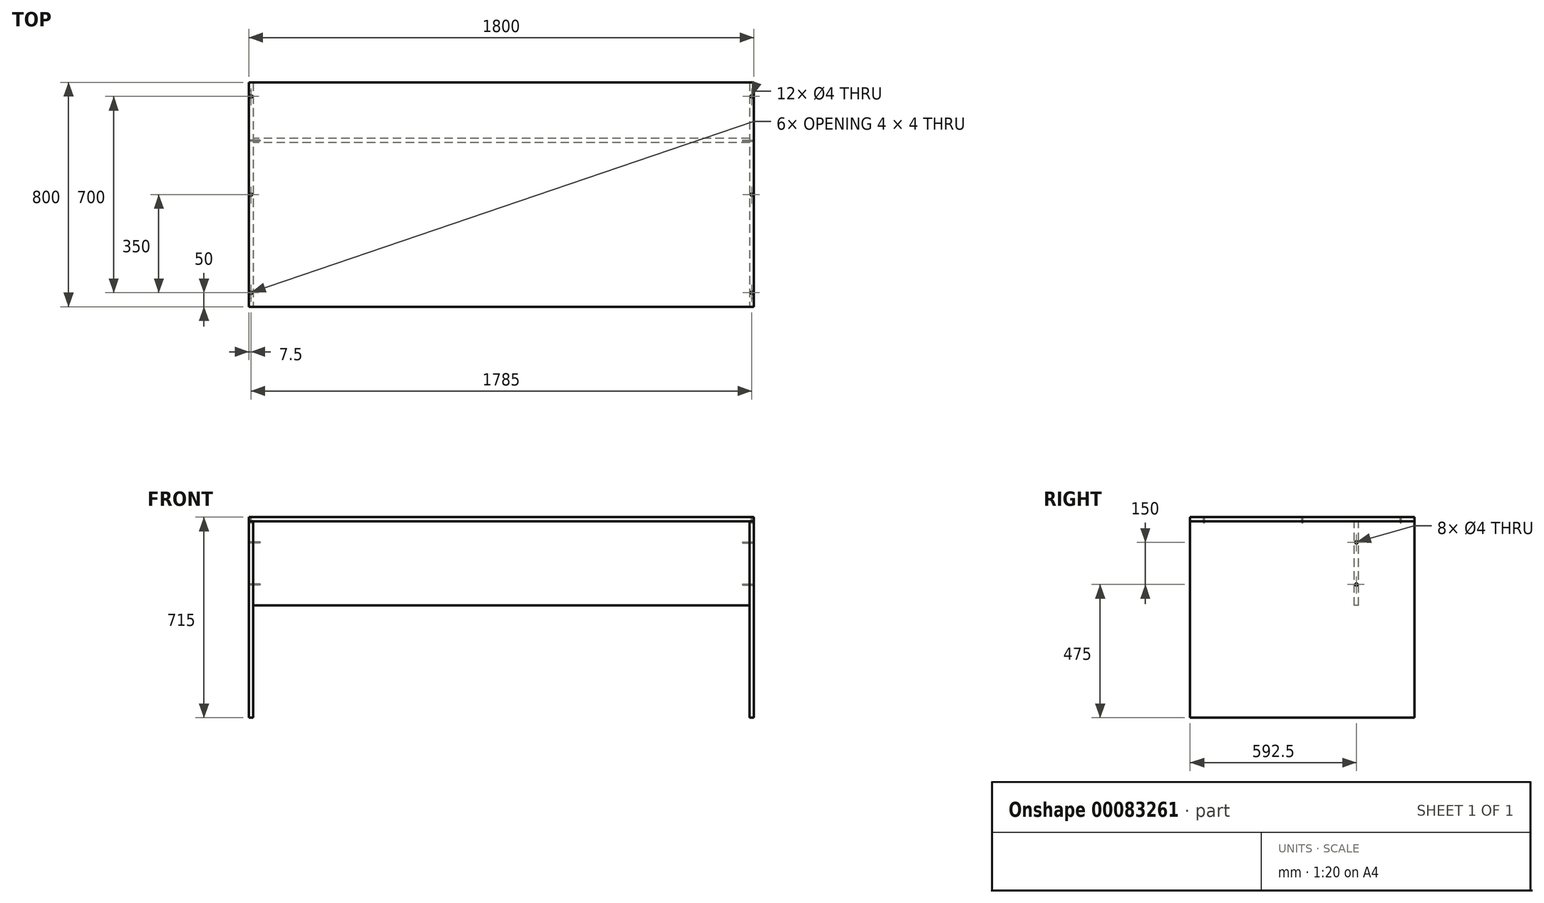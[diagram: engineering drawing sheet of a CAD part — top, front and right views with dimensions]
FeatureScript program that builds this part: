
annotation { "Feature Type Name" : "Feature", "Feature Type Description" : "" }
export const myFeature = defineFeature(function(context is Context, id is Id, definition is map)
    precondition{}
    {
        {
            var Q0;
            Q0=qCreatedBy(makeId("Front.planeOp"),FACE);
            var sketch = newSketch(context, id + "F0", { "sketchPlane" : qUnion([Q0])});
            skLineSegment(sketch, "E0.bottom", {"start": v(0, 0) * mm, "end": v(15, 0) * mm});
            skLineSegment(sketch, "E0.top", {"start": v(0, -700) * mm, "end": v(15, -700) * mm});
            skLineSegment(sketch, "E0.left", {"start": v(0, 0) * mm, "end": v(0, -700) * mm});
            skLineSegment(sketch, "E0.right", {"start": v(15, 0) * mm, "end": v(15, -700) * mm});
            skLineSegment(sketch, "E1.bottom", {"start": v(0, 0) * mm, "end": v(1800, 0) * mm});
            skLineSegment(sketch, "E1.top", {"start": v(0, 15) * mm, "end": v(1800, 15) * mm});
            skLineSegment(sketch, "E1.left", {"start": v(0, 0) * mm, "end": v(0, 15) * mm});
            skLineSegment(sketch, "E1.right", {"start": v(1800, 0) * mm, "end": v(1800, 15) * mm});
            skLineSegment(sketch, "E2", {"start": v(900, 0) * mm, "end": v(900, -515.89) * mm, "construction": true});
            skLineSegment(sketch, "E3.MirrorCS", {"start": v(1800, -700) * mm, "end": v(1785, -700) * mm});
            skLineSegment(sketch, "E4.MirrorCS", {"start": v(1785, 0) * mm, "end": v(1785, -700) * mm});
            skLineSegment(sketch, "E5.MirrorCS", {"start": v(1800, 0) * mm, "end": v(1800, -700) * mm});
            skSolve(sketch);
        }
        {
            var Q0;
            Q0=makeQuery(id+"F0.imprint","IMPRINT",FACE,{"disambiguationData":[TD([[makeQuery(id+"F0.imprint","IMPRINT",EDGE,{"derivedFrom":sQuery(id+"F0.wireOp",EDGE,"E1.top")}),-1.0]])]});
            extrude(context, id + "F1", {"entities" : qUnion([Q0]), "oppositeDirection" : true, "depth" : 800 * mm});
        }
        {
            var Q0;
            Q0=makeQuery(id+"F0.imprint","IMPRINT",FACE,{"disambiguationData":[TD([[makeQuery(id+"F0.imprint","IMPRINT",EDGE,{"derivedFrom":sQuery(id+"F0.wireOp",EDGE,"E0.top")}),1.0]])]});
            var Q1;
            Q1=makeQuery(id+"F0.imprint","IMPRINT",FACE,{"disambiguationData":[TD([[makeQuery(id+"F0.imprint","IMPRINT",EDGE,{"derivedFrom":sQuery(id+"F0.wireOp",EDGE,"E3.MirrorCS")}),-1.0]])]});
            extrude(context, id + "F2", {"entities" : qUnion([Q0, Q1]), "oppositeDirection" : true, "depth" : 800 * mm});
        }
        {
            var Q0;
            Q0=makeQuery(id+"F1.opExtrude","SWEPT_FACE",FACE,{"disambiguationData":[OSD([sQuery(id+"F0.wireOp",EDGE,"E1.bottom")])]});
            var sketch = newSketch(context, id + "F3", { "sketchPlane" : qUnion([Q0])});
            skLineSegment(sketch, "E6.0", {"start": v(15, -800) * mm, "end": v(15, 0) * mm, "construction": true});
            skLineSegment(sketch, "E6.1", {"start": v(1785, -800) * mm, "end": v(1785, 0) * mm});
            skLineSegment(sketch, "E7.0", {"start": v(0, 0) * mm, "end": v(1800, 0) * mm, "construction": true});
            skLineSegment(sketch, "E8.bottom", {"start": v(1785, -600) * mm, "end": v(15, -600) * mm});
            skLineSegment(sketch, "E8.top", {"start": v(1785, -585) * mm, "end": v(15, -585) * mm});
            skLineSegment(sketch, "E8.left", {"start": v(1785, -600) * mm, "end": v(1785, -585) * mm});
            skLineSegment(sketch, "E8.right", {"start": v(15, -600) * mm, "end": v(15, -585) * mm});
            skSolve(sketch);
        }
        {
            var Q0;
            Q0=makeQuery(id+"F3.imprint","IMPRINT",FACE,{"disambiguationData":[TD([[makeQuery(id+"F3.imprint","IMPRINT",EDGE,{"derivedFrom":sQuery(id+"F3.wireOp",EDGE,"E8.bottom")}),-1.0]])]});
            extrude(context, id + "F4", {"entities" : qUnion([Q0]), "depth" : 300 * mm});
        }
        {
            var Q0;
            Q0=makeQuery(id+"F1.opExtrude","SWEPT_FACE",FACE,{"disambiguationData":[OSD([sQuery(id+"F0.wireOp",EDGE,"E1.top")])]});
            var sketch = newSketch(context, id + "F5", { "sketchPlane" : qUnion([Q0])});
            skLineSegment(sketch, "E9.0.0", {"start": v(0, 0) * mm, "end": v(1800, 0) * mm});
            skLineSegment(sketch, "E9.0.1", {"start": v(1800, 0) * mm, "end": v(1800, 800) * mm});
            skLineSegment(sketch, "E9.0.2", {"start": v(1800, 800) * mm, "end": v(0, 800) * mm});
            skLineSegment(sketch, "E9.0.3", {"start": v(0, 800) * mm, "end": v(0, 0) * mm});
            skLineSegment(sketch, "E10", {"start": v(900, 800) * mm, "end": v(900, 0) * mm, "construction": true});
            skLineSegment(sketch, "E11.0", {"start": v(15, 800) * mm, "end": v(15, 0) * mm});
            skLineSegment(sketch, "E12.0", {"start": v(1785, 800) * mm, "end": v(1785, 0) * mm});
            skLineSegment(sketch, "E13.0", {"start": v(1785, 600) * mm, "end": v(15, 600) * mm});
            skLineSegment(sketch, "E13.1", {"start": v(1785, 585) * mm, "end": v(15, 585) * mm});
            skLineSegment(sketch, "E14", {"start": v(7.5, 800) * mm, "end": v(7.5, 0) * mm, "construction": true});
            skPoint(sketch, "E15", {"position": v(7.5, 750) * mm});
            skPoint(sketch, "E16", {"position": v(7.5, 50) * mm});
            skPoint(sketch, "E17", {"position": v(7.5, 400) * mm});
            skPoint(sketch, "E18.MirrorP", {"position": v(1792.5, 750) * mm});
            skPoint(sketch, "E19.MirrorP", {"position": v(1792.5, 400) * mm});
            skPoint(sketch, "E20.MirrorP", {"position": v(1792.5, 50) * mm});
            skSolve(sketch);
        }
        {
            var Q0;
            Q0=sQuery(id+"F5.wireOp",VERTEX,"E15");
            var Q1;
            Q1=sQuery(id+"F5.wireOp",VERTEX,"E17");
            var Q2;
            Q2=sQuery(id+"F5.wireOp",VERTEX,"E16");
            var Q3;
            Q3=sQuery(id+"F5.wireOp",VERTEX,"E18.MirrorP");
            var Q4;
            Q4=sQuery(id+"F5.wireOp",VERTEX,"E19.MirrorP");
            var Q5;
            Q5=sQuery(id+"F5.wireOp",VERTEX,"E20.MirrorP");
            var Q6;
            Q6=makeQuery(id+"F2.opExtrude","SWEPT_BODY",BODY,{"disambiguationData":[OSD([sQuery(id+"F0.wireOp",EDGE,"E0.top"),sQuery(id+"F0.wireOp",EDGE,"E0.left"),sQuery(id+"F0.wireOp",EDGE,"E0.right"),sQuery(id+"F0.wireOp",EDGE,"E1.bottom")])]});
            var Q7;
            Q7=makeQuery(id+"F2.opExtrude","SWEPT_BODY",BODY,{"disambiguationData":[OSD([sQuery(id+"F0.wireOp",EDGE,"E1.bottom"),sQuery(id+"F0.wireOp",EDGE,"E3.MirrorCS"),sQuery(id+"F0.wireOp",EDGE,"E4.MirrorCS"),sQuery(id+"F0.wireOp",EDGE,"E5.MirrorCS")])]});
            var Q8;
            Q8=makeQuery(id+"F1.opExtrude","SWEPT_BODY",BODY,{"disambiguationData":[OSD([sQuery(id+"F0.wireOp",EDGE,"E1.bottom"),sQuery(id+"F0.wireOp",EDGE,"E1.top"),sQuery(id+"F0.wireOp",EDGE,"E1.left"),sQuery(id+"F0.wireOp",EDGE,"E1.right")])]});
            hole(context, id + "F6", {"style" : HoleStyle.C_SINK, "endStyle" : HoleEndStyle.BLIND, "holeDiameter" : 4 * mm, "cSinkDiameter" : 8.96 * mm, "cSinkAngle" : 90 * degree, "holeDepth" : 20 * mm, "locations" : qUnion([Q0, Q1, Q2, Q3, Q4, Q5]), "scope" : qUnion([Q6, Q7, Q8])});
        }
        {
            var Q0;
            Q0=makeQuery(id+"F2.opExtrude","SWEPT_FACE",FACE,{"disambiguationData":[OSD([sQuery(id+"F0.wireOp",EDGE,"E0.left")])]});
            var sketch = newSketch(context, id + "F7", { "sketchPlane" : qUnion([Q0])});
            skLineSegment(sketch, "E21.0", {"start": v(-600, -300) * mm, "end": v(-585, -300) * mm});
            skLineSegment(sketch, "E21.1", {"start": v(-585, -300) * mm, "end": v(-585, 0) * mm});
            skLineSegment(sketch, "E21.2", {"start": v(-600, -300) * mm, "end": v(-600, 0) * mm});
            skLineSegment(sketch, "E21.3", {"start": v(-600, 0) * mm, "end": v(-585, 0) * mm});
            skLineSegment(sketch, "E22", {"start": v(-592.5, 0) * mm, "end": v(-592.5, -300) * mm, "construction": true});
            skPoint(sketch, "E23", {"position": v(-592.5, -75) * mm});
            skPoint(sketch, "E24", {"position": v(-592.5, -225) * mm});
            skSolve(sketch);
        }
        {
            var Q0;
            Q0=sQuery(id+"F7.wireOp",VERTEX,"E23");
            var Q1;
            Q1=sQuery(id+"F7.wireOp",VERTEX,"E24");
            var Q2;
            Q2=sQuery(id+"F9.wireOp",VERTEX,"E25.5");
            var Q3;
            Q3=sQuery(id+"F9.wireOp",VERTEX,"E25.6");
            var Q4;
            Q4=makeQuery(id+"F2.opExtrude","SWEPT_BODY",BODY,{"disambiguationData":[OSD([sQuery(id+"F0.wireOp",EDGE,"E0.top"),sQuery(id+"F0.wireOp",EDGE,"E0.left"),sQuery(id+"F0.wireOp",EDGE,"E0.right"),sQuery(id+"F0.wireOp",EDGE,"E1.bottom")])]});
            var Q5;
            Q5=makeQuery(id+"F4.opExtrude","SWEPT_BODY",BODY,{"disambiguationData":[OSD([sQuery(id+"F3.wireOp",EDGE,"E8.bottom"),sQuery(id+"F3.wireOp",EDGE,"E8.top"),sQuery(id+"F3.wireOp",EDGE,"E8.left"),sQuery(id+"F3.wireOp",EDGE,"E8.right")])]});
            hole(context, id + "F8", {"style" : HoleStyle.C_SINK, "endStyle" : HoleEndStyle.BLIND, "holeDiameter" : 4 * mm, "cSinkDiameter" : 8.96 * mm, "cSinkAngle" : 90 * degree, "holeDepth" : 40 * mm, "locations" : qUnion([Q0, Q1, Q2, Q3]), "scope" : qUnion([Q4, Q5])});
        }
        {
            var Q0;
            Q0=makeQuery(id+"F2.opExtrude","SWEPT_FACE",FACE,{"disambiguationData":[OSD([sQuery(id+"F0.wireOp",EDGE,"E5.MirrorCS")])]});
            var sketch = newSketch(context, id + "F9", { "sketchPlane" : qUnion([Q0])});
            skLineSegment(sketch, "E25.1", {"start": v(600, -300) * mm, "end": v(600, 0) * mm});
            skLineSegment(sketch, "E25.2", {"start": v(592.5, 0) * mm, "end": v(592.5, -300) * mm, "construction": true});
            skLineSegment(sketch, "E25.3", {"start": v(585, -300) * mm, "end": v(585, 0) * mm});
            skLineSegment(sketch, "E25.4", {"start": v(600, 0) * mm, "end": v(585, 0) * mm});
            skPoint(sketch, "E25.5", {"position": v(592.5, -75) * mm});
            skPoint(sketch, "E25.6", {"position": v(592.5, -225) * mm});
            skLineSegment(sketch, "E25.7", {"start": v(600, -300) * mm, "end": v(585, -300) * mm});
            skSolve(sketch);
        }
        {
            var Q0;
            Q0=sQuery(id+"F9.wireOp",VERTEX,"E25.5");
            var Q1;
            Q1=sQuery(id+"F9.wireOp",VERTEX,"E25.6");
            var Q2;
            Q2=makeQuery(id+"F2.opExtrude","SWEPT_BODY",BODY,{"disambiguationData":[OSD([sQuery(id+"F0.wireOp",EDGE,"E1.bottom"),sQuery(id+"F0.wireOp",EDGE,"E3.MirrorCS"),sQuery(id+"F0.wireOp",EDGE,"E4.MirrorCS"),sQuery(id+"F0.wireOp",EDGE,"E5.MirrorCS")])]});
            var Q3;
            Q3=makeQuery(id+"F4.opExtrude","SWEPT_BODY",BODY,{"disambiguationData":[OSD([sQuery(id+"F3.wireOp",EDGE,"E8.bottom"),sQuery(id+"F3.wireOp",EDGE,"E8.top"),sQuery(id+"F3.wireOp",EDGE,"E8.left"),sQuery(id+"F3.wireOp",EDGE,"E8.right")])]});
            hole(context, id + "F10", {"style" : HoleStyle.C_SINK, "endStyle" : HoleEndStyle.BLIND, "holeDiameter" : 4 * mm, "cSinkDiameter" : 8.96 * mm, "cSinkAngle" : 90 * degree, "holeDepth" : 40 * mm, "locations" : qUnion([Q0, Q1]), "scope" : qUnion([Q2, Q3])});
        }
        {
            var Q0;
            Q0=makeQuery(id+"F2.opExtrude","SWEPT_FACE",FACE,{"disambiguationData":[OSD([sQuery(id+"F0.wireOp",EDGE,"E0.top")])]});
            var sketch = newSketch(context, id + "F11", { "sketchPlane" : qUnion([Q0])});
            skLineSegment(sketch, "E26.0", {"start": v(0, 0) * mm, "end": v(15, 0) * mm});
            skLineSegment(sketch, "E26.1", {"start": v(15, -800) * mm, "end": v(15, 0) * mm});
            skLineSegment(sketch, "E26.2", {"start": v(0, -800) * mm, "end": v(0, 0) * mm});
            skLineSegment(sketch, "E26.3", {"start": v(0, -800) * mm, "end": v(15, -800) * mm});
            skLineSegment(sketch, "E27.0", {"start": v(1800, 0) * mm, "end": v(1785, 0) * mm});
            skLineSegment(sketch, "E27.1", {"start": v(1800, -800) * mm, "end": v(1800, 0) * mm});
            skLineSegment(sketch, "E27.2", {"start": v(1785, -800) * mm, "end": v(1785, 0) * mm});
            skLineSegment(sketch, "E27.3", {"start": v(1800, -800) * mm, "end": v(1785, -800) * mm});
            skLineSegment(sketch, "E28", {"start": v(7.5, 0) * mm, "end": v(7.5, -800) * mm, "construction": true});
            skLineSegment(sketch, "E29", {"start": v(1792.5, 0) * mm, "end": v(1792.5, -800) * mm, "construction": true});
            skPoint(sketch, "E30", {"position": v(7.5, -30) * mm});
            skPoint(sketch, "E31", {"position": v(7.5, -770) * mm});
            skPoint(sketch, "E32", {"position": v(1792.5, -30) * mm});
            skPoint(sketch, "E33", {"position": v(1792.5, -770) * mm});
            skSolve(sketch);
        }
        {
            var Q0;
            Q0=sQuery(id+"F11.wireOp",VERTEX,"E32");
            var Q1;
            Q1=sQuery(id+"F11.wireOp",VERTEX,"E33");
            var Q2;
            Q2=sQuery(id+"F11.wireOp",VERTEX,"E30");
            var Q3;
            Q3=sQuery(id+"F11.wireOp",VERTEX,"E31");
            var Q4;
            Q4=makeQuery(id+"F2.opExtrude","SWEPT_BODY",BODY,{"disambiguationData":[OSD([sQuery(id+"F0.wireOp",EDGE,"E0.top"),sQuery(id+"F0.wireOp",EDGE,"E0.left"),sQuery(id+"F0.wireOp",EDGE,"E0.right"),sQuery(id+"F0.wireOp",EDGE,"E1.bottom")])]});
            var Q5;
            Q5=makeQuery(id+"F2.opExtrude","SWEPT_BODY",BODY,{"disambiguationData":[OSD([sQuery(id+"F0.wireOp",EDGE,"E1.bottom"),sQuery(id+"F0.wireOp",EDGE,"E3.MirrorCS"),sQuery(id+"F0.wireOp",EDGE,"E4.MirrorCS"),sQuery(id+"F0.wireOp",EDGE,"E5.MirrorCS")])]});
            hole(context, id + "F12", {"style" : HoleStyle.SIMPLE, "endStyle" : HoleEndStyle.BLIND, "holeDiameter" : 3 * mm, "holeDepth" : 1 * mm, "locations" : qUnion([Q0, Q1, Q2, Q3]), "scope" : qUnion([Q4, Q5])});
        }
    });
